# Revit family: PUHY-P800YSNW-A1
name_source: partatom
category: Mechanical Equipment
revit_build: Autodesk Revit 2016 (Build: 20150220_1215(x64)
units: mm (PartAtom-declared; Revit-internal decimal feet)

## family parameters
Always vertical = Yes
Cut with Voids When Loaded = No
OmniClass Number = 23.75.00.00
OmniClass Title = Climate Control (HVAC)
Part Type = Normal
Room Calculation Point = No
Round Connector Dimension = Use Radius
Shared = No
Work Plane-Based = No

## types (6) — shared parameters
Airflow Rate (m3/h) = 34500
Airflow Rate (m3/min) = 575
Compressor Motor Output (kW) = 20.3
Compressor_Lubricant = MEL32
Compressor_Quantity = 2
Compressor_Type = Inverter scroll hermetic compressor
Cooling Capacity (kW) = 90
Cooling EER (kW/kW) = 3.42
Cooling Power Input (kW) = 26.31
Cooling SEER (kW/kW) = 6.48
Depth = 740 mm  [stored 2.42782 ft]
External Finish = Pre-coated galvanized steel sheets (+powder coating for -BS type) <MUNSELL 3Y 7.8/1.1 or similar>
Fan Motor Output (kW) = 1.84
Fan_Quantity = 4
Fan_Type = Propeller Fan
Gas pipe_radius = 17.465 mm  [stored 0.0572999 ft]
Heating COP (Nominal) (kW/kW) = 4.29
Heating COP (kW/kW) = 4.02
Heating Capacity (Nominal) (kW) = 90
Heating Capacity (kW) = 100
Heating Power Input (Nominal) (kW) = 20.97
Heating Power Input (kW) = 24.87
Heating SCOP (kW/kW) = 3.88
Height = 1858 mm  [stored 6.0958 ft]
Indoor Unit Model/Quantity = P10 to P250/2 to 50
Indoor Unit Total Capacity = 50 to 130% of outdoor unit capacity
Liquid pipe_radius = 9.525 mm  [stored 0.03125 ft]
Manufacturer = Mitsubishi Electric Corporation
Maximum Circuit Ampacity (A) = 63.5
Model = PUHY-P800YSNW-A1
Note_1 = Refrigerant pipe diameters may change depending on the installation condition. Please refer to the installation manual.
Outdoor unit 1 Breaker size (A) = 60
Outdoor unit 2 Breaker size (A) = 40
Phase = 3
Protection Devices_High pressure (MPa) = High pressure sensor, High pressure switch at 4.15
Protection Devices_Inverter circuit (COMP./FAN) = Over-current protection
Refrigerant Charge (kg) = 20.6
Refrigerant type = R410A
Sound Pressure Level (dB(A)) Cooling mode = 67.5
Sound Pressure Level (dB(A)) Heating mode = 71
Space View = Yes
Subcategory = HVAC
Temp. range of cooling (Indoor temp.) (W.B.) = 15.0 to 24.0
Temp. range of cooling (Outdoor temp.) (D.B.) = -5.0 to 52.0
Temp. range of heating (Indoor temp.) (D.B.) = 15.0 to 27.0
Temp. range of heating (Outdoor temp.) (W.B.) = -20.0 to 15.5
URL = http://www.mitsubishielectric.com
Unit Weight (kg) = 570
Width = 2510 mm  [stored 8.23491 ft]
zero-valued in all types: Equip_No., External static pressure (Pa), SerialNumber, TagNumber

## per-type parameters (varying)
| type | Cooling Current Input (A) | Cooling Rated Load Ampacity (A) | Heating Current Input (A) | Heating Current Input (Nominal) (A) | Heating Rated Load Ampacity (A) | Hertz | Voltage |
| PUHY-P800YSNW-A1_380V_50Hz | 44.4 | 44.4 | 41.9 | 35.4 | 41.9 | 50 Hz | 380 V |
| PUHY-P800YSNW-A1_380V_60Hz | 44.4 | 44.4 | 41.9 | 35.4 | 41.9 | 60 Hz | 380 V |
| PUHY-P800YSNW-A1_400V_50Hz | 42.1 | 42.1 | 39.8 | 33.6 | 39.8 | 50 Hz | 400 V |
| PUHY-P800YSNW-A1_400V_60Hz | 42.1 | 42.1 | 39.8 | 33.6 | 39.8 | 60 Hz | 400 V |
| PUHY-P800YSNW-A1_415V_50Hz | 40.6 | 40.6 | 38.4 | 32.4 | 38.4 | 50 Hz | 415 V |
| PUHY-P800YSNW-A1_415V_60Hz | 40.6 | 40.6 | 38.4 | 32.4 | 38.4 | 60 Hz | 415 V |

note: [stored X ft] marks values corroborated as IEEE doubles in the binary element streams (Revit-internal decimal feet)

## geometry (parser evidence)
native form markers: Blend x62, Sweep x10
no freeform markers — native parametric forms only
